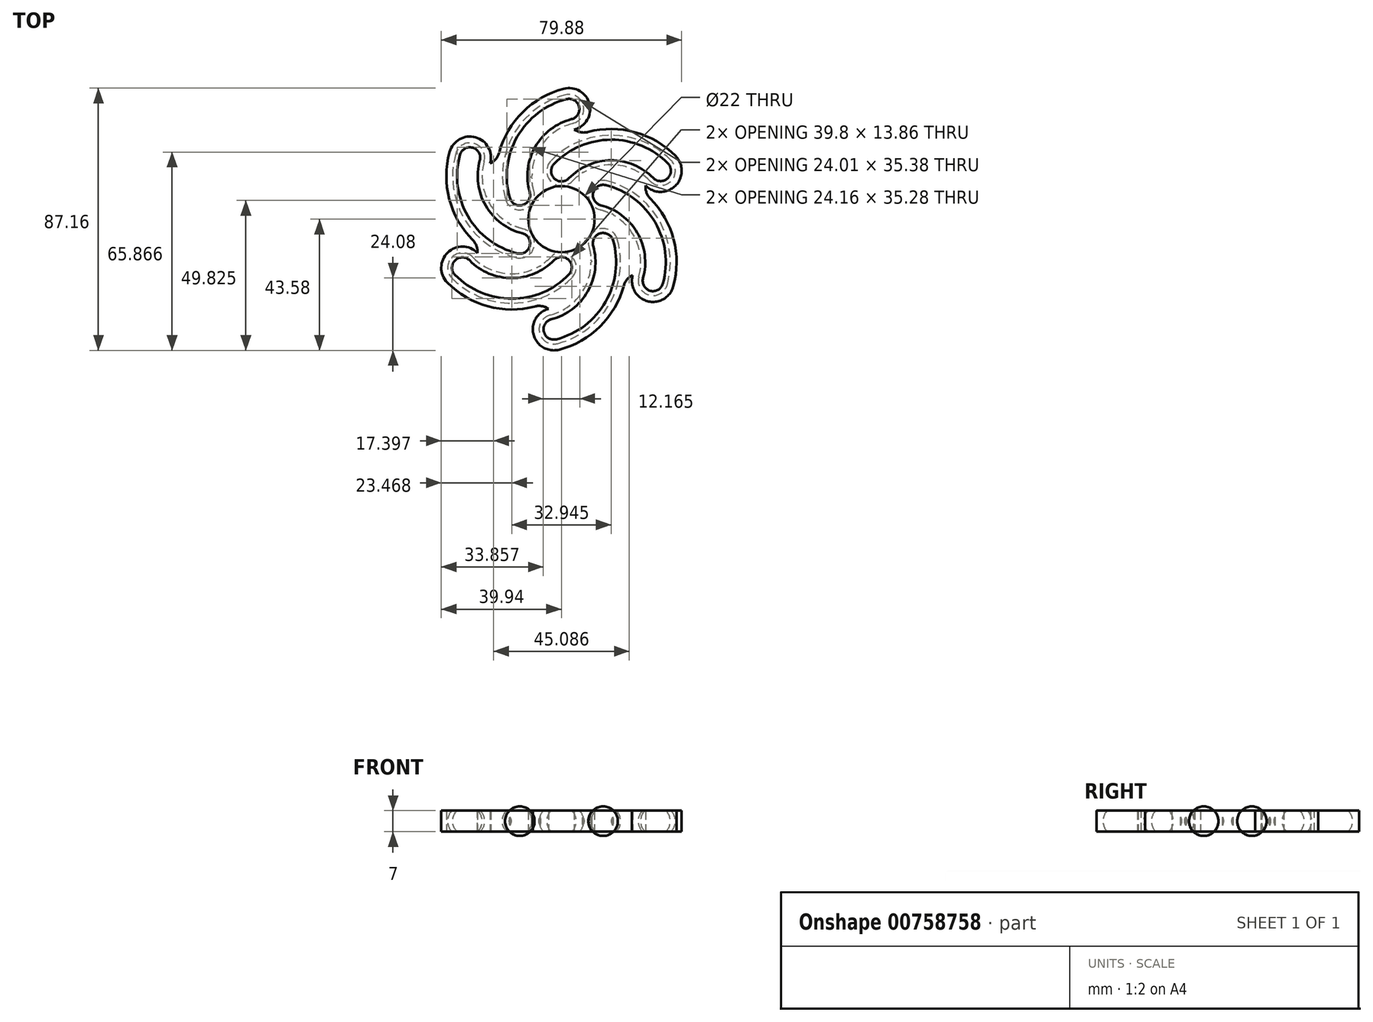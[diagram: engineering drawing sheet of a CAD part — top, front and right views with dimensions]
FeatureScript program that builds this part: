
annotation { "Feature Type Name" : "Feature", "Feature Type Description" : "" }
export const myFeature = defineFeature(function(context is Context, id is Id, definition is map)
    precondition{}
    {
        {
            var Q0;
            Q0=qCreatedBy(makeId("Top.planeOp"),FACE);
            var sketch = newSketch(context, id + "F0", { "sketchPlane" : qUnion([Q0])});
            skArc(sketch, "E0", {"start": v(7, 8.49) * mm, "mid": v(0, 11) * mm, "end": v(-7, 8.49) * mm});
            skPoint(sketch, "E1", {"position": v(0, -24.5) * mm});
            skLineSegment(sketch, "E2", {"start": v(0, 0) * mm, "end": v(0, 16) * mm, "construction": true});
            skArc(sketch, "E3", {"start": v(27.95, 11.2) * mm, "mid": v(14.86, 15.91) * mm, "end": v(3.03, 8.6) * mm});
            skArc(sketch, "E4.0", {"start": v(32.94, 16.1) * mm, "mid": v(16.45, 23) * mm, "end": v(0, 16) * mm});
            skArc(sketch, "E5.0", {"start": v(37.94, 21) * mm, "mid": v(12.16, 29.68) * mm, "end": v(-10.04, 13.95) * mm});
            skArc(sketch, "E6", {"start": v(27.95, 11.2) * mm, "mid": v(37.85, 11.1) * mm, "end": v(37.94, 21) * mm});
            skLineSegment(sketch, "E7", {"start": v(-7, 8.49) * mm, "end": v(-10.04, 13.95) * mm});
            skArc(sketch, "E8.0", {"start": v(10.18, 12.34) * mm, "mid": v(0, 16) * mm, "end": v(-10.18, 12.34) * mm});
            skArc(sketch, "E9.0", {"start": v(26.1, 9.38) * mm, "mid": v(15.13, 13.33) * mm, "end": v(5.22, 7.2) * mm});
            skLineSegment(sketch, "E10", {"start": v(26.1, 9.38) * mm, "end": v(27.95, 11.2) * mm});
            skSolve(sketch);
        }
        {
            var Q0;
            {var subQ4=sQuery(id+"F0.wireOp",EDGE,"PiiM7Q08-lsxY-islm-UEzh-ksM0SnnuY6FK");Q0=makeQuery(id+"F0.imprint","IMPRINT",FACE,{"disambiguationData":[TD([[makeQuery(id+"F0.imprint","IMPRINT",EDGE,{"derivedFrom":subQ4}),-1.0]])]});}
            var Q1;
            Q1=makeQuery(id+"F0.imprint","IMPRINT",FACE,{"disambiguationData":[TD([[makeQuery(id+"F0.imprint","IMPRINT",EDGE,{"derivedFrom":sQuery(id+"F0.wireOp",EDGE,"E0")}),-1.0]])]});
            var Q2;
            {var subQ4=sQuery(id+"F0.wireOp",EDGE,"QqK0a54Q-URX9-TbrE-nkqz-KXdzGL0UVco7");Q2=makeQuery(id+"F0.imprint","IMPRINT",FACE,{"disambiguationData":[TD([[makeQuery(id+"F0.imprint","IMPRINT",EDGE,{"derivedFrom":subQ4}),-1.0]])]});}
            var Q3;
            {var subQ5=sQuery(id+"F0.wireOp",EDGE,"PiiM7Q08-lsxY-islm-UEzh-ksM0SnnuY6FK");Q3=makeQuery(id+"F0.imprint","IMPRINT",FACE,{"disambiguationData":[TD([[makeQuery(id+"F0.imprint","IMPRINT",EDGE,{"derivedFrom":subQ5}),1.0]])]});}
            var Q4;
            {var subQ1=sQuery(id+"F0.wireOp",EDGE,"E5.0");Q4=makeQuery(id+"F0.imprint","IMPRINT",FACE,{"disambiguationData":[TD([[makeQuery(id+"F0.imprint","IMPRINT",EDGE,{"derivedFrom":subQ1}),1.0]])]});}
            extrude(context, id + "F1", {"entities" : qUnion([Q0, Q1, Q2, Q3, Q4]), "endBound" : BoundingType.SYMMETRIC, "depth" : 7 * mm, "offsetDistance" : 25 * mm});
        }
        {
            var Q0;
            Q0=makeQuery(id+"F1.opExtrude","SWEPT_EDGE",EDGE,{"disambiguationData":[OSD([sQuery(id+"F0.wireOp",EDGE,"E3"),sQuery(id+"F0.wireOp",EDGE,"E6")])]});
            var Q1;
            Q1=sQuery(id+"F0.wireOp",VERTEX,"E5.0.start");
            cPlane(context, id + "F2", {"entities" : qUnion([Q0, Q1]), "cplaneType" : CPlaneType.LINE_ANGLE, "offset" : 25 * mm, "angle" : 0 * degree, "width" : 150 * mm, "height" : 150 * mm});
        }
        {
            var Q0;
            Q0=qCreatedBy(id+"F2.planeOp",FACE);
            var sketch = newSketch(context, id + "F3", { "sketchPlane" : qUnion([Q0])});
            skLineSegment(sketch, "E11", {"start": v(34.8, 4.9) * mm, "end": v(34.8, -4.9) * mm});
            skArc(sketch, "E12", {"start": v(34.8, -4.9) * mm, "mid": v(39.7, 0) * mm, "end": v(34.8, 4.9) * mm});
            skArc(sketch, "E13.MirrorCS", {"start": v(34.8, -4.9) * mm, "mid": v(29.9, 0) * mm, "end": v(34.8, 4.9) * mm});
            skSolve(sketch);
        }
        {
            var Q0;
            Q0=makeQuery(id+"F3.imprint","IMPRINT",FACE,{"disambiguationData":[TD([[makeQuery(id+"F3.imprint","IMPRINT",EDGE,{"derivedFrom":sQuery(id+"F3.wireOp",EDGE,"E11")}),1.0]])]});
            var Q1;
            Q1=makeQuery(id+"F3.imprint","IMPRINT",FACE,{"disambiguationData":[TD([[makeQuery(id+"F3.imprint","IMPRINT",EDGE,{"derivedFrom":sQuery(id+"F3.wireOp",EDGE,"E11")}),-1.0]])]});
            var Q2;
            Q2=sQuery(id+"F0.wireOp",EDGE,"E4.0");
            sweep(context, id + "F4", {"operationType" : NewBodyOperationType.REMOVE, "profiles" : qUnion([Q0, Q1]), "path" : qUnion([Q2])});
        }
        {
            var Q0;
            Q0=makeQuery(id+"F3.imprint","IMPRINT",FACE,{"disambiguationData":[TD([[makeQuery(id+"F3.imprint","IMPRINT",EDGE,{"derivedFrom":sQuery(id+"F3.wireOp",EDGE,"E11")}),1.0]])]});
            var Q1;
            Q1=sQuery(id+"F3.wireOp",EDGE,"E11");
            revolve(context, id + "F5", {"operationType" : NewBodyOperationType.REMOVE, "surfaceOperationType" : NewSurfaceOperationType.NEW, "entities" : qUnion([Q0]), "axis" : qUnion([Q1]), "revolveType" : RevolveType.ONE_DIRECTION, "angle" : 180 * degree});
        }
        {
            var Q0;
            Q0=makeQuery(id+"F4.boolean.opBoolean","COPY",FACE,{"derivedFrom":makeQuery(id+"F4.opSweep","CAP_FACE",FACE,{"disambiguationData":[OSD([sQuery(id+"F0.wireOp",VERTEX,"E4.0.end"),sQuery(id+"F3.wireOp",EDGE,"E12"),sQuery(id+"F3.wireOp",EDGE,"E13.MirrorCS")])],"isStart":false})});
            var sketch = newSketch(context, id + "F6", { "sketchPlane" : qUnion([Q0])});
            skLineSegment(sketch, "E14", {"start": v(16.03, 0) * mm, "end": v(6.23, 0) * mm});
            skArc(sketch, "E15", {"start": v(6.23, 0) * mm, "mid": v(11.13, -4.9) * mm, "end": v(16.03, 0) * mm});
            skSolve(sketch);
        }
        {
            var Q0;
            {var subQ1=makeQuery(id+"F4.boolean.opBoolean","INTERSECT",EDGE,{"derivedFrom":[makeQuery(id+"F1.opExtrude","CAP_FACE",FACE,{"disambiguationData":[OSD([sQuery(id+"F0.wireOp",EDGE,"E0"),sQuery(id+"F0.wireOp",EDGE,"Lb8NWhK4-ym9p-KzVv-z8Fr-7k6zUVGv0M9w"),sQuery(id+"F0.wireOp",EDGE,"QqK0a54Q-URX9-TbrE-nkqz-KXdzGL0UVco7"),sQuery(id+"F0.wireOp",EDGE,"E3"),sQuery(id+"F0.wireOp",EDGE,"E5.0"),sQuery(id+"F0.wireOp",EDGE,"E6"),sQuery(id+"F0.wireOp",EDGE,"E7")])],"isStart":true}),makeQuery(id+"F4.opSweep","CAP_FACE",FACE,{"disambiguationData":[OSD([sQuery(id+"F0.wireOp",VERTEX,"I2wmlmdm-DSrS-oub0-GOcV-EtuJTHkaWZzk.end"),sQuery(id+"F3.wireOp",EDGE,"E12"),sQuery(id+"F3.wireOp",EDGE,"E13.MirrorCS")])],"isStart":false})]});Q0=makeQuery(id+"F6.imprint","IMPRINT",FACE,{"disambiguationData":[TD([[makeQuery(id+"F6.imprint","IMPRINT",EDGE,{"derivedFrom":subQ1}),-1.0]])]});}
            var Q1;
            {var subQ0=sQuery(id+"F6.wireOp",EDGE,"E14");Q1=makeQuery(id+"F6.imprint","IMPRINT",FACE,{"disambiguationData":[TD([[makeQuery(id+"F6.imprint","IMPRINT",EDGE,{"derivedFrom":subQ0}),1.0]])]});}
            var Q2;
            Q2=sQuery(id+"F6.wireOp",EDGE,"E14");
            revolve(context, id + "F7", {"operationType" : NewBodyOperationType.REMOVE, "surfaceOperationType" : NewSurfaceOperationType.NEW, "entities" : qUnion([Q0, Q1]), "axis" : qUnion([Q2]), "revolveType" : RevolveType.FULL, "oppositeDirection" : true});
        }
        {
            var Q0;
            Q0=qCreatedBy(makeId("Front.planeOp"),FACE);
            var sketch = newSketch(context, id + "F8", { "sketchPlane" : qUnion([Q0])});
            skLineSegment(sketch, "E16", {"start": v(0, -9.37) * mm, "end": v(0, 10.86) * mm, "construction": true});
            skSolve(sketch);
        }
        {
            var Q0;
            Q0=makeQuery(id+"F1.opExtrude","SWEPT_BODY",BODY,{"disambiguationData":[OSD([sQuery(id+"F0.wireOp",EDGE,"E0"),sQuery(id+"F0.wireOp",EDGE,"Lb8NWhK4-ym9p-KzVv-z8Fr-7k6zUVGv0M9w"),sQuery(id+"F0.wireOp",EDGE,"QqK0a54Q-URX9-TbrE-nkqz-KXdzGL0UVco7"),sQuery(id+"F0.wireOp",EDGE,"E3"),sQuery(id+"F0.wireOp",EDGE,"E5.0"),sQuery(id+"F0.wireOp",EDGE,"E6"),sQuery(id+"F0.wireOp",EDGE,"E7")])]});
            var Q1;
            Q1=sQuery(id+"F8.wireOp",EDGE,"E16");
            circularPattern(context, id + "F9", {"operationType" : NewBodyOperationType.ADD, "entities" : qUnion([Q0]), "axis" : qUnion([Q1]), "angle" : 360 * degree, "instanceCount" : 6, "equalSpace" : true});
        }
        {
            var Q0;
            Q0=makeQuery(id+"F9.boolean.opBoolean","INTERSECT",EDGE,{"derivedFrom":[makeQuery(id+"F1.opExtrude","SWEPT_FACE",FACE,{"disambiguationData":[OSD([sQuery(id+"F0.wireOp",EDGE,"E10")])]}),makeQuery(id+"F9.opPattern","COPY",FACE,{"derivedFrom":makeQuery(id+"F1.opExtrude","SWEPT_FACE",FACE,{"disambiguationData":[OSD([sQuery(id+"F0.wireOp",EDGE,"E5.0")])]}),"instanceName":"5"})]});
            var Q1;
            Q1=makeQuery(id+"F9.boolean.opBoolean","INTERSECT",EDGE,{"derivedFrom":[makeQuery(id+"F9.opPattern","COPY",FACE,{"derivedFrom":makeQuery(id+"F1.opExtrude","SWEPT_FACE",FACE,{"disambiguationData":[OSD([sQuery(id+"F0.wireOp",EDGE,"E5.0")])]}),"instanceName":"4"}),makeQuery(id+"F9.opPattern","COPY",FACE,{"derivedFrom":makeQuery(id+"F1.opExtrude","SWEPT_FACE",FACE,{"disambiguationData":[OSD([sQuery(id+"F0.wireOp",EDGE,"E10")])]}),"instanceName":"5"})]});
            var Q2;
            Q2=makeQuery(id+"F9.boolean.opBoolean","INTERSECT",EDGE,{"derivedFrom":[makeQuery(id+"F9.opPattern","COPY",FACE,{"derivedFrom":makeQuery(id+"F1.opExtrude","SWEPT_FACE",FACE,{"disambiguationData":[OSD([sQuery(id+"F0.wireOp",EDGE,"E5.0")])]}),"instanceName":"3"}),makeQuery(id+"F9.opPattern","COPY",FACE,{"derivedFrom":makeQuery(id+"F1.opExtrude","SWEPT_FACE",FACE,{"disambiguationData":[OSD([sQuery(id+"F0.wireOp",EDGE,"E10")])]}),"instanceName":"4"})]});
            var Q3;
            Q3=makeQuery(id+"F9.boolean.opBoolean","INTERSECT",EDGE,{"derivedFrom":[makeQuery(id+"F9.opPattern","COPY",FACE,{"derivedFrom":makeQuery(id+"F1.opExtrude","SWEPT_FACE",FACE,{"disambiguationData":[OSD([sQuery(id+"F0.wireOp",EDGE,"E5.0")])]}),"instanceName":"2"}),makeQuery(id+"F9.opPattern","COPY",FACE,{"derivedFrom":makeQuery(id+"F1.opExtrude","SWEPT_FACE",FACE,{"disambiguationData":[OSD([sQuery(id+"F0.wireOp",EDGE,"E10")])]}),"instanceName":"3"})]});
            var Q4;
            Q4=makeQuery(id+"F9.boolean.opBoolean","INTERSECT",EDGE,{"derivedFrom":[makeQuery(id+"F9.opPattern","COPY",FACE,{"derivedFrom":makeQuery(id+"F1.opExtrude","SWEPT_FACE",FACE,{"disambiguationData":[OSD([sQuery(id+"F0.wireOp",EDGE,"E5.0")])]}),"instanceName":"1"}),makeQuery(id+"F9.opPattern","COPY",FACE,{"derivedFrom":makeQuery(id+"F1.opExtrude","SWEPT_FACE",FACE,{"disambiguationData":[OSD([sQuery(id+"F0.wireOp",EDGE,"E10")])]}),"instanceName":"2"})]});
            var Q5;
            Q5=makeQuery(id+"F9.boolean.opBoolean","INTERSECT",EDGE,{"derivedFrom":[makeQuery(id+"F1.opExtrude","SWEPT_FACE",FACE,{"disambiguationData":[OSD([sQuery(id+"F0.wireOp",EDGE,"E5.0")])]}),makeQuery(id+"F9.opPattern","COPY",FACE,{"derivedFrom":makeQuery(id+"F1.opExtrude","SWEPT_FACE",FACE,{"disambiguationData":[OSD([sQuery(id+"F0.wireOp",EDGE,"E10")])]}),"instanceName":"1"})]});
            fillet(context, id + "F10", {"entities" : qUnion([Q0, Q1, Q2, Q3, Q4, Q5]), "radius" : 5.45 * mm, "tangentPropagation" : true, "allowEdgeOverflow" : false});
        }
    });
